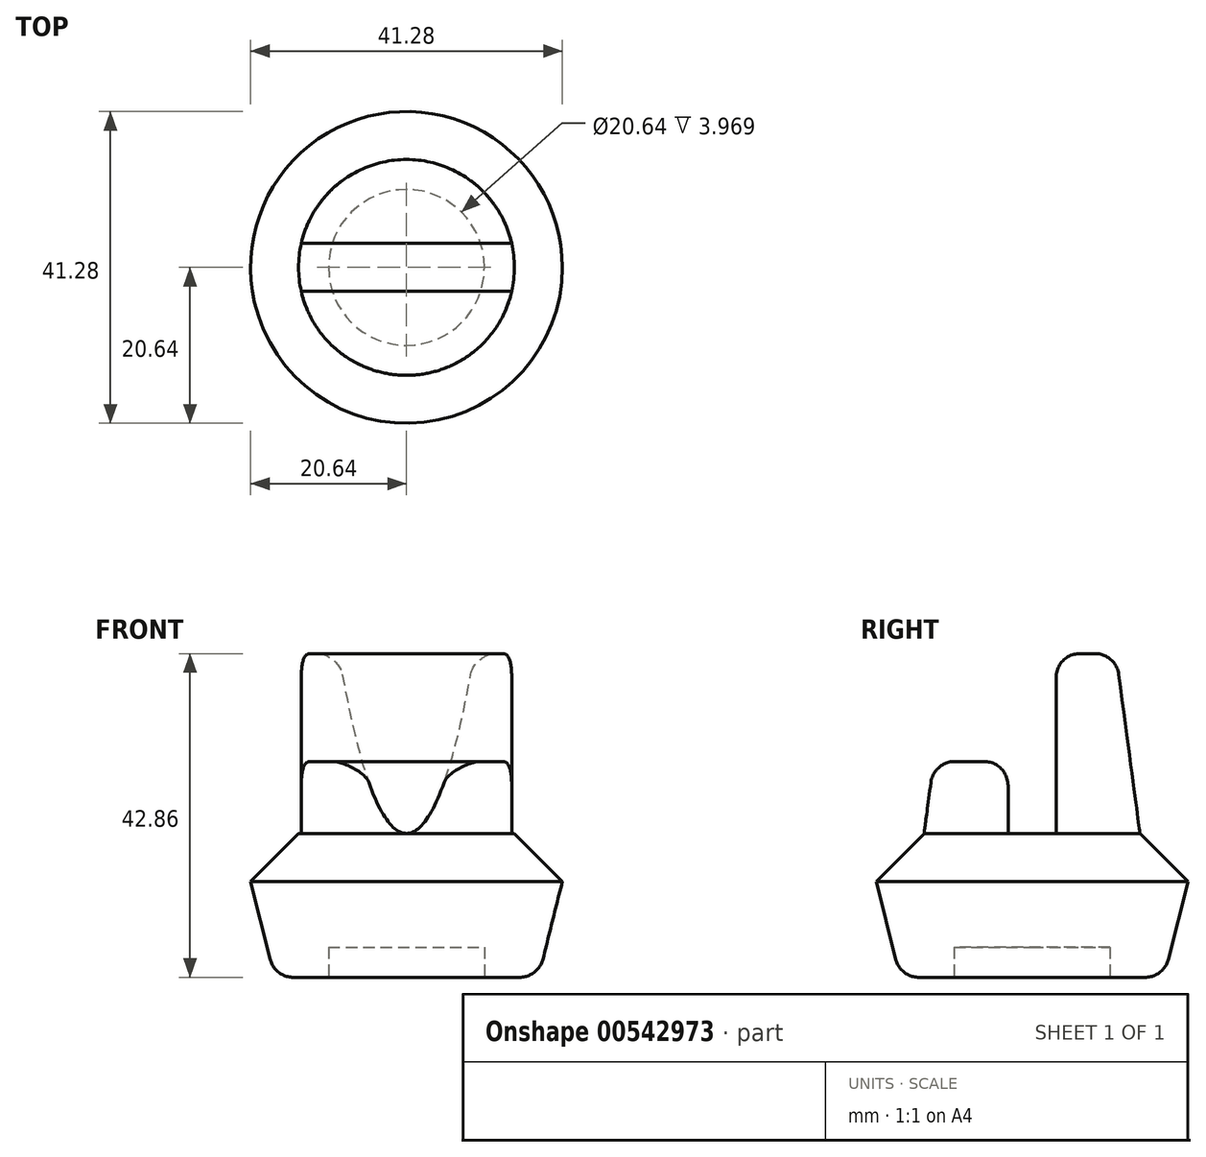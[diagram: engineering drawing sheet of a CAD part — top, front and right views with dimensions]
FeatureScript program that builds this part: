
annotation { "Feature Type Name" : "Feature", "Feature Type Description" : "" }
export const myFeature = defineFeature(function(context is Context, id is Id, definition is map)
    precondition{}
    {
        {
            var Q0;
            Q0=qCreatedBy(makeId("Front.planeOp"),FACE);
            var sketch = newSketch(context, id + "F0", { "sketchPlane" : qUnion([Q0])});
            skLineSegment(sketch, "E0", {"start": v(0, 19.05) * mm, "end": v(0, 0) * mm});
            skLineSegment(sketch, "E1", {"start": v(0, 0) * mm, "end": v(17.46, 0) * mm});
            skLineSegment(sketch, "E2", {"start": v(17.46, 0) * mm, "end": v(20.64, 12.7) * mm});
            skLineSegment(sketch, "E3", {"start": v(20.64, 12.7) * mm, "end": v(14.29, 19.05) * mm});
            skLineSegment(sketch, "E4", {"start": v(14.29, 19.05) * mm, "end": v(0, 19.05) * mm});
            skSolve(sketch);
        }
        {
            var Q0;
            Q0=makeQuery(id+"F0.imprint","IMPRINT",FACE,{"disambiguationData":[TD([[makeQuery(id+"F0.imprint","IMPRINT",EDGE,{"derivedFrom":sQuery(id+"F0.wireOp",EDGE,"E0")}),1.0]])]});
            var Q1;
            Q1=sQuery(id+"F0.wireOp",EDGE,"E0");
            revolve(context, id + "F1", {"surfaceOperationType" : NewSurfaceOperationType.NEW, "entities" : qUnion([Q0]), "axis" : qUnion([Q1]), "revolveType" : RevolveType.FULL});
        }
        {
            var Q0;
            Q0=qCreatedBy(makeId("Right.planeOp"),FACE);
            var sketch = newSketch(context, id + "F2", { "sketchPlane" : qUnion([Q0])});
            skLineSegment(sketch, "E5.0", {"start": v(-14.29, 19.05) * mm, "end": v(14.29, 19.05) * mm, "construction": true});
            skLineSegment(sketch, "E6", {"start": v(-13.02, 28.57) * mm, "end": v(-14.29, 19.05) * mm});
            skLineSegment(sketch, "E7", {"start": v(-13.02, 28.58) * mm, "end": v(-3.18, 28.58) * mm});
            skLineSegment(sketch, "E8", {"start": v(-3.17, 28.58) * mm, "end": v(-3.18, 19.05) * mm});
            skLineSegment(sketch, "E9", {"start": v(3.18, 19.05) * mm, "end": v(3.18, 42.86) * mm});
            skLineSegment(sketch, "E10", {"start": v(3.17, 42.86) * mm, "end": v(11.11, 42.86) * mm});
            skLineSegment(sketch, "E11", {"start": v(14.29, 19.05) * mm, "end": v(11.11, 42.86) * mm});
            skLineSegment(sketch, "E12", {"start": v(0, 0) * mm, "end": v(0, 51.88) * mm, "construction": true});
            skLineSegment(sketch, "E13", {"start": v(-3.18, 19.05) * mm, "end": v(-14.29, 19.05) * mm});
            skLineSegment(sketch, "E14", {"start": v(3.18, 19.05) * mm, "end": v(14.29, 19.05) * mm});
            skSolve(sketch);
        }
        {
            var Q0;
            Q0=makeQuery(id+"F1.opRevolve","SWEPT_FACE",FACE,{"disambiguationData":[OSD([sQuery(id+"F0.wireOp",EDGE,"E1")])]});
            var sketch = newSketch(context, id + "F3", { "sketchPlane" : qUnion([Q0])});
            skCircle(sketch, "E15", {"center": v(0, 0) * mm, "radius": 10.32 * mm});
            skSolve(sketch);
        }
        {
            var Q0;
            Q0 = qSketchRegion(id + "F3", true);
            extrude(context, id + "F4", {"entities" : qUnion([Q0]), "operationType" : NewBodyOperationType.REMOVE, "oppositeDirection" : true, "depth" : 3.97 * mm, "offsetDistance" : 25.4 * mm});
        }
        {
            var Q0;
            Q0 = qSketchRegion(id + "F2", true);
            extrude(context, id + "F5", {"entities" : qUnion([Q0]), "operationType" : NewBodyOperationType.ADD, "depth" : 31.75 * mm, "offsetDistance" : 25.4 * mm, "symmetric" : true});
        }
        {
            var Q0;
            Q0=makeQuery(id+"F1.opRevolve","SWEPT_FACE",FACE,{"disambiguationData":[OSD([sQuery(id+"F0.wireOp",EDGE,"E4")])]});
            var sketch = newSketch(context, id + "F6", { "sketchPlane" : qUnion([Q0])});
            skArc(sketch, "E16.0", {"start": v(13.93, -3.18) * mm, "mid": v(14.29, 0) * mm, "end": v(13.93, 3.18) * mm});
            skArc(sketch, "E16.2", {"start": v(0, -14.29) * mm, "mid": v(8.9, -11.17) * mm, "end": v(13.93, -3.18) * mm});
            skArc(sketch, "E16.3", {"start": v(-13.93, -3.17) * mm, "mid": v(-8.9, -11.17) * mm, "end": v(0, -14.29) * mm});
            skArc(sketch, "E16.4", {"start": v(-13.93, 3.17) * mm, "mid": v(-14.29, 0) * mm, "end": v(-13.93, -3.17) * mm});
            skArc(sketch, "E16.5", {"start": v(0, 14.29) * mm, "mid": v(-8.9, 11.17) * mm, "end": v(-13.93, 3.18) * mm});
            skArc(sketch, "E16.6", {"start": v(13.93, 3.18) * mm, "mid": v(8.9, 11.17) * mm, "end": v(0, 14.29) * mm});
            skCircle(sketch, "E17", {"center": v(0, 0) * mm, "radius": 25.4 * mm});
            skSolve(sketch);
        }
        {
            var Q0;
            Q0 = qSketchRegion(id + "F6", true);
            extrude(context, id + "F7", {"entities" : qUnion([Q0]), "operationType" : NewBodyOperationType.REMOVE, "depth" : 25.4 * mm, "offsetDistance" : 25.4 * mm});
        }
        {
            var Q0;
            Q0=makeQuery(id+"F5.opExtrude","SWEPT_EDGE",EDGE,{"disambiguationData":[OSD([sQuery(id+"F2.wireOp",EDGE,"E9"),sQuery(id+"F2.wireOp",EDGE,"E10")])]});
            var Q1;
            Q1=makeQuery(id+"F5.opExtrude","SWEPT_EDGE",EDGE,{"disambiguationData":[OSD([sQuery(id+"F2.wireOp",EDGE,"E7"),sQuery(id+"F2.wireOp",EDGE,"E8")])]});
            var Q2;
            Q2=makeQuery(id+"F5.opExtrude","SWEPT_EDGE",EDGE,{"disambiguationData":[OSD([sQuery(id+"F2.wireOp",EDGE,"E10"),sQuery(id+"F2.wireOp",EDGE,"E11")])]});
            var Q3;
            Q3=makeQuery(id+"F5.opExtrude","SWEPT_EDGE",EDGE,{"disambiguationData":[OSD([sQuery(id+"F2.wireOp",EDGE,"E6"),sQuery(id+"F2.wireOp",EDGE,"E7")])]});
            var Q4;
            {var subQ0=sQuery(id+"F2.wireOp",EDGE,"E9");Q4=makeQuery(id+"F5.boolean.opBoolean","SPLIT",EDGE,{"disambiguationData":[topologyDisambiguationEdgeConnected([makeQuery(id+"F1.opRevolve","SWEPT_FACE",FACE,{"disambiguationData":[OSD([sQuery(id+"F0.wireOp",EDGE,"E4")])]}),makeQuery(id+"F5.opExtrude","SWEPT_FACE",FACE,{"disambiguationData":[OSD([subQ0])]})])],"derivedFrom":makeQuery(id+"F5.opExtrude","SWEPT_EDGE",EDGE,{"disambiguationData":[OSD([subQ0,sQuery(id+"F2.wireOp",EDGE,"E14")])]})});}
            var Q5;
            {var subQ0=sQuery(id+"F2.wireOp",EDGE,"E8");Q5=makeQuery(id+"F5.boolean.opBoolean","SPLIT",EDGE,{"disambiguationData":[topologyDisambiguationEdgeConnected([makeQuery(id+"F1.opRevolve","SWEPT_FACE",FACE,{"disambiguationData":[OSD([sQuery(id+"F0.wireOp",EDGE,"E4")])]}),makeQuery(id+"F5.opExtrude","SWEPT_FACE",FACE,{"disambiguationData":[OSD([subQ0])]})])],"derivedFrom":makeQuery(id+"F5.opExtrude","SWEPT_EDGE",EDGE,{"disambiguationData":[OSD([subQ0,sQuery(id+"F2.wireOp",EDGE,"E13")])]})});}
            var Q6;
            Q6=makeQuery(id+"F1.opRevolve","SWEPT_EDGE",EDGE,{"disambiguationData":[OSD([sQuery(id+"F0.wireOp",EDGE,"E1"),sQuery(id+"F0.wireOp",EDGE,"E2")])]});
            fillet(context, id + "F8", {"entities" : qUnion([Q0, Q1, Q2, Q3, Q4, Q5, Q6]), "tangentPropagation" : true, "radius" : 3.17 * mm, "defaultsChanged" : false, "vertexSettings" : [], "allowEdgeOverflow" : false});
        }
    });
